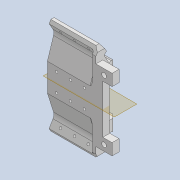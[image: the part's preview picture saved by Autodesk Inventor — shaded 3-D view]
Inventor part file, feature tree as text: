
AUTODESK INVENTOR PART (.ipt)
format: ipt  version: 2020 (Build 240168000, 168)  size: 520,192 bytes
history: native  units: mm
features: reference x17, projected_geometry x16, sketch x13, extrude x11, thicken_offset x7, fillet x6, other x5, plane x3, mirror x3, hole x2, chamfer x2
ambient origin geometry x8: Origin, YZ Plane, XZ Plane, XY Plane, X Axis, Y Axis, Z Axis, Center Point
bodies: Solid1 (feature_tree)
feature tree (85):
  sketch  "Sketch1"  dims[d0=5.0mm d1=7.0mm]
  plane  "Work Plane1"
  extrude  "Extrusion1"  Depth=7.0mm
  sketch  "Sketch2"  dims[d2=5.0mm d3=7.0mm]
  plane  "Work Plane2"
  extrude  "Extrusion2"  Depth=7.0mm
  hole  "Hole1"  [1 undecoded]
  plane  "Work Plane3"
  mirror  "Mirror1"
  extrude  "Extrusion3"  Depth=10.0mm
  thicken_offset  "Thicken1"
  thicken_offset  "Thicken2"
  thicken_offset  "Thicken3"
  extrude  "Extrusion4"  Depth=10.0mm
  extrude  "Extrusion5"  Depth=20.0mm TaperAngle=0.0deg
  thicken_offset  "Thicken4"
  thicken_offset  "Thicken5"
  extrude  "Extrusion6"  Depth=1.0mm
  extrude  "Extrusion7"  Depth=1.0mm
  fillet  "Fillet2"  Radius=1.0mm
  fillet  "Fillet3"  Radius=1.0mm
  fillet  "Fillet4"  Radius=2.9mm
  thicken_offset  "Thicken6"
  thicken_offset  "Thicken7"
  fillet  "Fillet5"  Radius=1.45mm
  chamfer  "Chamfer1"  Distance=21.5mm
  extrude  "Extrusion8"  Depth=1.0mm
  fillet  "Fillet6"  Radius=1.0mm
  chamfer  "Chamfer2"  Distance=20.0mm
  extrude  "Extrusion9"  Depth=1.0mm
  fillet  "Fillet7"  Radius=0.5mm
  mirror  "Mirror2"
  hole  "Hole2"  [1 undecoded]
  extrude  "Extrusion10"  Depth=1.0mm
  extrude  "Extrusion11"  Depth=1.0mm TaperAngle=0.0deg
  mirror  "Mirror3"
  reference  "Reference1"
  reference  "Reference2"
  reference  "Reference3"
  reference  "Reference4"
  reference  "Reference5"
  reference  "Reference6"
  reference  "Reference7"
  reference  "Reference8"
  reference  "Reference9"
  reference  "Reference10"
  reference  "Reference11"
  reference  "Reference12"
  reference  "Reference13"
  reference  "Reference14"
  projected_geometry  "Projected Loop1"
  sketch  "Sketch3"  dims[d4=3.0mm d5=21.0mm]
  reference  "Reference15"
  reference  "Reference16"
  reference  "Reference17"
  sketch  "Sketch4"  dims[d6=10.0mm d7=0.0mm d8=2.0mm]
  projected_geometry  "Projected Loop2"
  projected_geometry  "Projected Loop3"
  sketch  "Sketch5"  dims[d9=10.0mm d10=0.0mm]
  projected_geometry  "Projected Loop4"
  sketch  "Sketch6"  dims[d11=1.1mm d12=6.0mm d13=4.0mm d14=2.0mm d15=90.0deg d16=10.0mm d17=0.0mm d18=2.0mm]
  projected_geometry  "Projected Loop5"
  projected_geometry  "Projected Loop6"
  projected_geometry  "Projected Loop7"
  sketch  "Sketch7"  dims[d19=2.0mm d20=20.0mm d21=0.0mm]
  projected_geometry  "Projected Loop8"
  projected_geometry  "Projected Loop9"
  sketch  "Sketch8"  dims[d22=1.0mm d23=1.0mm]
  projected_geometry  "Projected Loop10"
  sketch  "Sketch9"  dims[d24=1.0mm d25=1.0mm d26=1.0mm d27=1.0mm d28=2.9mm d29=1.45mm]
  projected_geometry  "Projected Loop11"
  projected_geometry  "Projected Loop12"
  sketch  "Sketch10"  dims[d30=2.9mm]
  projected_geometry  "Projected Loop13"
  sketch  "Sketch11"  dims[d31=12.0mm d32=21.5mm d33=0.0mm]
  projected_geometry  "Projected Loop14"
  sketch  "Sketch12"  dims[d35=1.0mm d36=1.0mm d37=1.0mm]
  projected_geometry  "Projected Loop15"
  sketch  "Sketch13"  dims[d38=1.0mm d39=20.0mm d40=0.0mm d41=0.5mm d42=0.5mm d43=0.5mm d44=0.5mm d45=20.0mm d46=0.0mm d47=0.1mm d48=0.0mm d49=0.4mm d50=0.6mm d51=1.0mm d52=0.5mm d53=0.5mm d54=0.5mm d55=0.5mm d56=3.0mm d57=1.5mm d58=2.0mm d59=45.0deg d60=2.0mm d61=0.0mm d62=1.0mm d63=1.5mm d64=2.0mm d65=45.0deg d66=3.5mm d67=3.5mm d68=1.5mm d69=30.0mm d70=0.0mm d71=1.0mm d72=4.0mm d73=6.0mm d74=6.0mm d75=4.0mm d76=4.0mm d77=4.0mm d78=4.0mm d79=4.0mm d80=4.0mm d81=1.1mm d82=6.0mm d83=4.0mm d84=2.0mm d85=90.0deg d86=10.0mm d87=0.0mm d88=7.0mm d89=3.5mm d90=30.0mm d91=0.0mm d92=4.0mm d93=1.0mm d94=2.0mm d95=30.0mm d96=0.0mm]
  projected_geometry  "Projected Loop16"
  parser-record x1  (decoder bookkeeping rows leaked as tree rows — omitted from the tree; the rows remain in map.json)
  other  "tip_3_n_ass.iam"
  other  "end_shell_n_1:1"
  other  "bl_tube_ass_2:1"
  other  "bl_tube_hn_1:1"
note: 2 required parameter values undecoded (feature->parameter linkage not recoverable at this tier; creation-order binding heuristic only, values carry confidence <= 0.55)
note: 1 file-system path scrubbed to <path> (originals preserved in map.json)
